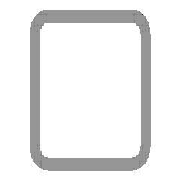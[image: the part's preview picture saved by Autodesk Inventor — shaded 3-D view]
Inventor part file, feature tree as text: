
AUTODESK INVENTOR PART (.ipt)
format: ipt  version: 2025.1 (Build 291241020, 241B)  size: 142,848 bytes
history: native  units: mm (DEFAULTED — no unit token found)
features: other x4, sketch x1, plane x1
ambient origin geometry x8: Origin, YZ Plane, XZ Plane, XY Plane, X Axis, Y Axis, Z Axis, Center Point
bodies: Solid1 (feature_tree), Body (feature_tree)
feature tree (6):
  parser-record x1  (decoder bookkeeping rows leaked as tree rows — omitted from the tree; the rows remain in map.json)
  other  "Driven Length"
  other  "Start Plane"
  other  "End Plane"
  sketch  "Sketch3"  dims[d3=790.0mm d4=0.0mm d7=4.0mm d9=40.0mm d11=40.0mm d12=2.0mm d13=100.0mm d14=890.0mm d15=20.0mm d16=20.0mm d17=90.0deg d18=790.0mm]
  plane  "Work Plane3"
